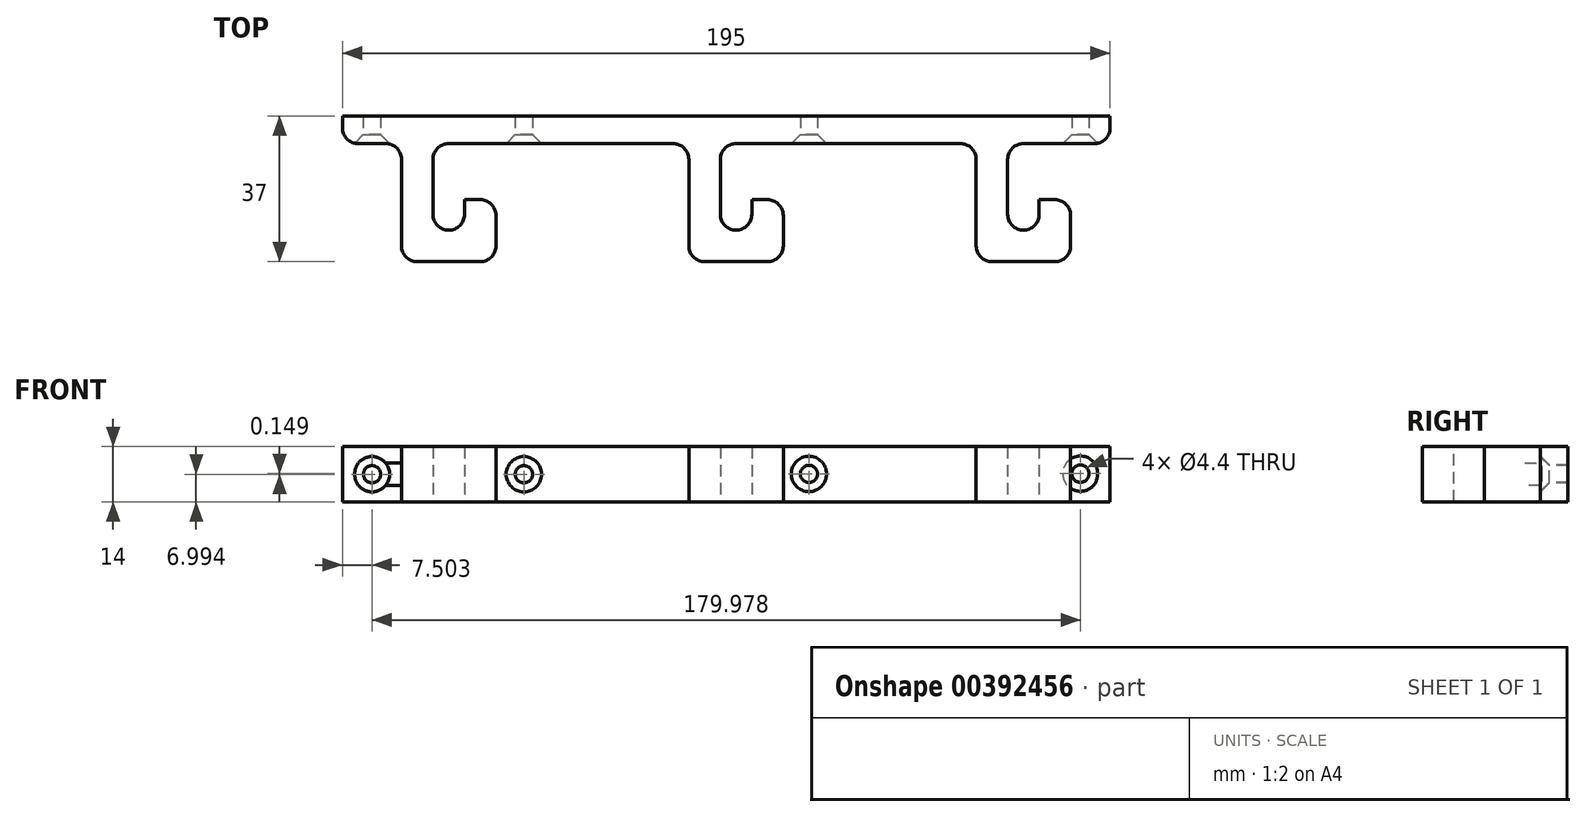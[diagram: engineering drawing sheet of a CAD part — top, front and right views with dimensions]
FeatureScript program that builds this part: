
annotation { "Feature Type Name" : "Feature", "Feature Type Description" : "" }
export const myFeature = defineFeature(function(context is Context, id is Id, definition is map)
    precondition{}
    {
        {
            var Q0;
            Q0=qCreatedBy(makeId("Top.planeOp"),FACE);
            var sketch = newSketch(context, id + "F0", { "sketchPlane" : qUnion([Q0])});
            skLineSegment(sketch, "E0.bottom", {"start": v(-95.94, 0) * mm, "end": v(99.06, 0) * mm});
            skLineSegment(sketch, "E0.top", {"start": v(-95.94, 7) * mm, "end": v(99.06, 7) * mm});
            skLineSegment(sketch, "E0.left", {"start": v(-95.94, 0) * mm, "end": v(-95.94, 7) * mm});
            skLineSegment(sketch, "E0.right", {"start": v(99.06, 0) * mm, "end": v(99.06, 7) * mm});
            skLineSegment(sketch, "E1", {"start": v(-80.94, 0) * mm, "end": v(-80.94, -30) * mm});
            skLineSegment(sketch, "E2", {"start": v(-80.94, -30) * mm, "end": v(-56.94, -30) * mm});
            skLineSegment(sketch, "E3", {"start": v(-56.94, -30) * mm, "end": v(-56.94, -14.25) * mm});
            skLineSegment(sketch, "E4", {"start": v(-56.94, -14.25) * mm, "end": v(-64.94, -14.25) * mm});
            skLineSegment(sketch, "E5", {"start": v(-64.94, -14.25) * mm, "end": v(-64.94, -22) * mm});
            skLineSegment(sketch, "E6", {"start": v(-64.94, -22) * mm, "end": v(-72.94, -22) * mm});
            skLineSegment(sketch, "E7", {"start": v(-72.94, -22) * mm, "end": v(-72.94, 0) * mm});
            skLineSegment(sketch, "E8.1.0.0", {"start": v(8.06, -22) * mm, "end": v(0.06, -22) * mm});
            skLineSegment(sketch, "E8.1.0.1", {"start": v(-7.94, 0) * mm, "end": v(-7.94, -30) * mm});
            skLineSegment(sketch, "E8.1.0.2", {"start": v(0.06, -22) * mm, "end": v(0.06, 0) * mm});
            skLineSegment(sketch, "E8.1.0.3", {"start": v(8.06, -14.25) * mm, "end": v(8.06, -22) * mm});
            skLineSegment(sketch, "E8.1.0.4", {"start": v(16.06, -14.25) * mm, "end": v(8.06, -14.25) * mm});
            skLineSegment(sketch, "E8.1.0.5", {"start": v(16.06, -30) * mm, "end": v(16.06, -14.25) * mm});
            skLineSegment(sketch, "E8.1.0.6", {"start": v(-7.94, -30) * mm, "end": v(16.06, -30) * mm});
            skLineSegment(sketch, "E8.2.0.0", {"start": v(81.06, -22) * mm, "end": v(73.06, -22) * mm});
            skLineSegment(sketch, "E8.2.0.1", {"start": v(65.06, 0) * mm, "end": v(65.06, -30) * mm});
            skLineSegment(sketch, "E8.2.0.2", {"start": v(73.06, -22) * mm, "end": v(73.06, 0) * mm});
            skLineSegment(sketch, "E8.2.0.3", {"start": v(81.06, -14.25) * mm, "end": v(81.06, -22) * mm});
            skLineSegment(sketch, "E8.2.0.4", {"start": v(89.06, -14.25) * mm, "end": v(81.06, -14.25) * mm});
            skLineSegment(sketch, "E8.2.0.5", {"start": v(89.06, -30) * mm, "end": v(89.06, -14.25) * mm});
            skLineSegment(sketch, "E8.2.0.6", {"start": v(65.06, -30) * mm, "end": v(89.06, -30) * mm});
            skLineSegment(sketch, "E8.direction1", {"start": v(-80.94, -30) * mm, "end": v(-7.94, -30) * mm, "construction": true});
            skSolve(sketch);
        }
        {
            var Q0;
            Q0=makeQuery(id+"F0.imprint","IMPRINT",FACE,{"disambiguationData":[TD([[makeQuery(id+"F0.imprint","IMPRINT",EDGE,{"derivedFrom":sQuery(id+"F0.wireOp",EDGE,"E0.top")}),-1.0]])]});
            var Q1;
            {var subQ0=sQuery(id+"F0.wireOp",EDGE,"E1");Q1=makeQuery(id+"F0.imprint","IMPRINT",FACE,{"disambiguationData":[TD([[makeQuery(id+"F0.imprint","IMPRINT",EDGE,{"derivedFrom":subQ0}),1.0]])]});}
            var Q2;
            Q2=makeQuery(id+"F0.imprint","IMPRINT",FACE,{"disambiguationData":[TD([[makeQuery(id+"F0.imprint","IMPRINT",EDGE,{"derivedFrom":sQuery(id+"F0.wireOp",EDGE,"E8.1.0.0")}),1.0]])]});
            var Q3;
            Q3=makeQuery(id+"F0.imprint","IMPRINT",FACE,{"disambiguationData":[TD([[makeQuery(id+"F0.imprint","IMPRINT",EDGE,{"derivedFrom":sQuery(id+"F0.wireOp",EDGE,"E8.2.0.0")}),1.0]])]});
            extrude(context, id + "F1", {"entities" : qUnion([Q0, Q1, Q2, Q3]), "depth" : 14 * mm});
        }
        {
            var Q0;
            {var subQ0=sQuery(id+"F0.wireOp",EDGE,"E0.bottom");Q0=makeQuery(id+"F1.opExtrude","SWEPT_FACE",FACE,{"disambiguationData":[OSD([subQ0]),TDD([makeQuery(id+"F0.imprint","IMPRINT",EDGE,{"disambiguationData":[TD([[makeQuery(id+"F0.imprint","INTERSECT",VERTEX,{"derivedFrom":[subQ0,sQuery(id+"F0.wireOp",EDGE,"E0.left")]}),-1.0]])],"derivedFrom":subQ0})])]});}
            var sketch = newSketch(context, id + "F2", { "sketchPlane" : qUnion([Q0])});
            skLineSegment(sketch, "E9", {"start": v(-95.94, 7) * mm, "end": v(-80.94, 7) * mm});
            skLineSegment(sketch, "E10", {"start": v(-88.44, 14) * mm, "end": v(-88.44, 0) * mm});
            skPoint(sketch, "E11", {"position": v(-88.44, 7) * mm});
            skLineSegment(sketch, "E12", {"start": v(-49.86, 13.99) * mm, "end": v(-49.86, 0) * mm});
            skPoint(sketch, "E13", {"position": v(-49.86, 7) * mm});
            skLineSegment(sketch, "E14", {"start": v(22.58, 14.14) * mm, "end": v(22.58, 0) * mm});
            skLineSegment(sketch, "E15", {"start": v(91.54, 14.29) * mm, "end": v(91.54, 0) * mm});
            skPoint(sketch, "E16", {"position": v(22.58, 7.07) * mm});
            skPoint(sketch, "E17", {"position": v(91.54, 7.14) * mm});
            skSolve(sketch);
        }
        {
            var Q0;
            Q0=sQuery(id+"F2.wireOp",VERTEX,"E11");
            var Q1;
            Q1=sQuery(id+"F2.wireOp",VERTEX,"E13");
            var Q2;
            Q2=sQuery(id+"F2.wireOp",VERTEX,"E16");
            var Q3;
            Q3=sQuery(id+"F2.wireOp",VERTEX,"E17");
            var Q4;
            Q4=makeQuery(id+"F1.opExtrude","SWEPT_BODY",BODY,{"disambiguationData":[OSD([sQuery(id+"F0.wireOp",EDGE,"E0.bottom"),sQuery(id+"F0.wireOp",EDGE,"E0.top"),sQuery(id+"F0.wireOp",EDGE,"E0.left"),sQuery(id+"F0.wireOp",EDGE,"E0.right"),sQuery(id+"F0.wireOp",EDGE,"E1"),sQuery(id+"F0.wireOp",EDGE,"E2"),sQuery(id+"F0.wireOp",EDGE,"E3"),sQuery(id+"F0.wireOp",EDGE,"E4"),sQuery(id+"F0.wireOp",EDGE,"E5"),sQuery(id+"F0.wireOp",EDGE,"E6"),sQuery(id+"F0.wireOp",EDGE,"E7"),sQuery(id+"F0.wireOp",EDGE,"E8.1.0.0"),sQuery(id+"F0.wireOp",EDGE,"E8.1.0.1"),sQuery(id+"F0.wireOp",EDGE,"E8.1.0.2"),sQuery(id+"F0.wireOp",EDGE,"E8.1.0.3"),sQuery(id+"F0.wireOp",EDGE,"E8.1.0.4"),sQuery(id+"F0.wireOp",EDGE,"E8.1.0.5"),sQuery(id+"F0.wireOp",EDGE,"E8.1.0.6"),sQuery(id+"F0.wireOp",EDGE,"E8.2.0.0"),sQuery(id+"F0.wireOp",EDGE,"E8.2.0.1"),sQuery(id+"F0.wireOp",EDGE,"E8.2.0.2"),sQuery(id+"F0.wireOp",EDGE,"E8.2.0.3"),sQuery(id+"F0.wireOp",EDGE,"E8.2.0.4"),sQuery(id+"F0.wireOp",EDGE,"E8.2.0.5"),sQuery(id+"F0.wireOp",EDGE,"E8.2.0.6")])]});
            hole(context, id + "F3", {"style" : HoleStyle.C_SINK, "endStyle" : HoleEndStyle.THROUGH, "standardTappedOrClearance" : lookupTablePath({ "standard" : "ISO", "fit" : "Normal", "size" : "M4", "type" : "Clearance" }), "standardBlindInLast" : lookupTablePath({ "fit" : "Standard", "standard" : "ISO", "size" : "M4", "type" : "Clearance" }), "holeDiameter" : 4.4 * mm, "cSinkDiameter" : 8.96 * mm, "cSinkAngle" : 90 * degree, "isTappedThrough" : true, "tappedDepth" : 12 * mm, "tapClearance" : 3, "locations" : qUnion([Q0, Q1, Q2, Q3]), "scope" : qUnion([Q4])});
        }
        {
            var Q0;
            Q0=makeQuery(id+"F1.opExtrude","SWEPT_EDGE",EDGE,{"disambiguationData":[OSD([sQuery(id+"F0.wireOp",EDGE,"E1"),sQuery(id+"F0.wireOp",EDGE,"E2")])]});
            var Q1;
            Q1=makeQuery(id+"F1.opExtrude","SWEPT_EDGE",EDGE,{"disambiguationData":[OSD([sQuery(id+"F0.wireOp",EDGE,"E2"),sQuery(id+"F0.wireOp",EDGE,"E3")])]});
            var Q2;
            Q2=makeQuery(id+"F1.opExtrude","SWEPT_EDGE",EDGE,{"disambiguationData":[OSD([sQuery(id+"F0.wireOp",EDGE,"E8.1.0.1"),sQuery(id+"F0.wireOp",EDGE,"E8.1.0.6")])]});
            var Q3;
            Q3=makeQuery(id+"F1.opExtrude","SWEPT_EDGE",EDGE,{"disambiguationData":[OSD([sQuery(id+"F0.wireOp",EDGE,"E8.1.0.5"),sQuery(id+"F0.wireOp",EDGE,"E8.1.0.6")])]});
            var Q4;
            Q4=makeQuery(id+"F1.opExtrude","SWEPT_EDGE",EDGE,{"disambiguationData":[OSD([sQuery(id+"F0.wireOp",EDGE,"E8.2.0.1"),sQuery(id+"F0.wireOp",EDGE,"E8.2.0.6")])]});
            var Q5;
            Q5=makeQuery(id+"F1.opExtrude","SWEPT_EDGE",EDGE,{"disambiguationData":[OSD([sQuery(id+"F0.wireOp",EDGE,"E8.2.0.5"),sQuery(id+"F0.wireOp",EDGE,"E8.2.0.6")])]});
            var Q6;
            Q6=makeQuery(id+"F1.opExtrude","SWEPT_EDGE",EDGE,{"disambiguationData":[OSD([sQuery(id+"F0.wireOp",EDGE,"E8.2.0.0"),sQuery(id+"F0.wireOp",EDGE,"E8.2.0.2")])]});
            var Q7;
            Q7=makeQuery(id+"F1.opExtrude","SWEPT_EDGE",EDGE,{"disambiguationData":[OSD([sQuery(id+"F0.wireOp",EDGE,"E8.2.0.0"),sQuery(id+"F0.wireOp",EDGE,"E8.2.0.3")])]});
            var Q8;
            Q8=makeQuery(id+"F1.opExtrude","SWEPT_EDGE",EDGE,{"disambiguationData":[OSD([sQuery(id+"F0.wireOp",EDGE,"E8.2.0.4"),sQuery(id+"F0.wireOp",EDGE,"E8.2.0.5")])]});
            var Q9;
            Q9=makeQuery(id+"F1.opExtrude","SWEPT_EDGE",EDGE,{"disambiguationData":[OSD([sQuery(id+"F0.wireOp",EDGE,"E8.1.0.4"),sQuery(id+"F0.wireOp",EDGE,"E8.1.0.5")])]});
            var Q10;
            Q10=makeQuery(id+"F1.opExtrude","SWEPT_EDGE",EDGE,{"disambiguationData":[OSD([sQuery(id+"F0.wireOp",EDGE,"E3"),sQuery(id+"F0.wireOp",EDGE,"E4")])]});
            var Q11;
            Q11=makeQuery(id+"F1.opExtrude","SWEPT_EDGE",EDGE,{"disambiguationData":[OSD([sQuery(id+"F0.wireOp",EDGE,"E8.1.0.0"),sQuery(id+"F0.wireOp",EDGE,"E8.1.0.3")])]});
            var Q12;
            Q12=makeQuery(id+"F1.opExtrude","SWEPT_EDGE",EDGE,{"disambiguationData":[OSD([sQuery(id+"F0.wireOp",EDGE,"E8.1.0.0"),sQuery(id+"F0.wireOp",EDGE,"E8.1.0.2")])]});
            var Q13;
            Q13=makeQuery(id+"F1.opExtrude","SWEPT_EDGE",EDGE,{"disambiguationData":[OSD([sQuery(id+"F0.wireOp",EDGE,"E5"),sQuery(id+"F0.wireOp",EDGE,"E6")])]});
            var Q14;
            Q14=makeQuery(id+"F1.opExtrude","SWEPT_EDGE",EDGE,{"disambiguationData":[OSD([sQuery(id+"F0.wireOp",EDGE,"E6"),sQuery(id+"F0.wireOp",EDGE,"E7")])]});
            var Q15;
            Q15=makeQuery(id+"F1.opExtrude","SWEPT_EDGE",EDGE,{"disambiguationData":[OSD([sQuery(id+"F0.wireOp",EDGE,"E0.bottom"),sQuery(id+"F0.wireOp",EDGE,"E8.1.0.2")])]});
            var Q16;
            Q16=makeQuery(id+"F1.opExtrude","SWEPT_EDGE",EDGE,{"disambiguationData":[OSD([sQuery(id+"F0.wireOp",EDGE,"E0.bottom"),sQuery(id+"F0.wireOp",EDGE,"E8.2.0.2")])]});
            var Q17;
            Q17=makeQuery(id+"F1.opExtrude","SWEPT_EDGE",EDGE,{"disambiguationData":[OSD([sQuery(id+"F0.wireOp",EDGE,"E0.bottom"),sQuery(id+"F0.wireOp",EDGE,"E8.2.0.1")])]});
            var Q18;
            Q18=makeQuery(id+"F1.opExtrude","SWEPT_EDGE",EDGE,{"disambiguationData":[OSD([sQuery(id+"F0.wireOp",EDGE,"E0.bottom"),sQuery(id+"F0.wireOp",EDGE,"E8.1.0.1")])]});
            var Q19;
            Q19=makeQuery(id+"F1.opExtrude","SWEPT_EDGE",EDGE,{"disambiguationData":[OSD([sQuery(id+"F0.wireOp",EDGE,"E0.bottom"),sQuery(id+"F0.wireOp",EDGE,"E1")])]});
            var Q20;
            Q20=makeQuery(id+"F1.opExtrude","SWEPT_EDGE",EDGE,{"disambiguationData":[OSD([sQuery(id+"F0.wireOp",EDGE,"E0.bottom"),sQuery(id+"F0.wireOp",EDGE,"E7")])]});
            var Q21;
            Q21=makeQuery(id+"F1.opExtrude","SWEPT_EDGE",EDGE,{"disambiguationData":[OSD([sQuery(id+"F0.wireOp",EDGE,"E0.bottom"),sQuery(id+"F0.wireOp",EDGE,"E0.right")])]});
            var Q22;
            Q22=makeQuery(id+"F1.opExtrude","SWEPT_EDGE",EDGE,{"disambiguationData":[OSD([sQuery(id+"F0.wireOp",EDGE,"E0.bottom"),sQuery(id+"F0.wireOp",EDGE,"E0.left")])]});
            fillet(context, id + "F4", {"entities" : qUnion([Q0, Q1, Q2, Q3, Q4, Q5, Q6, Q7, Q8, Q9, Q10, Q11, Q12, Q13, Q14, Q15, Q16, Q17, Q18, Q19, Q20, Q21, Q22]), "radius" : 4 * mm, "tangentPropagation" : true, "allowEdgeOverflow" : false});
        }
    });
